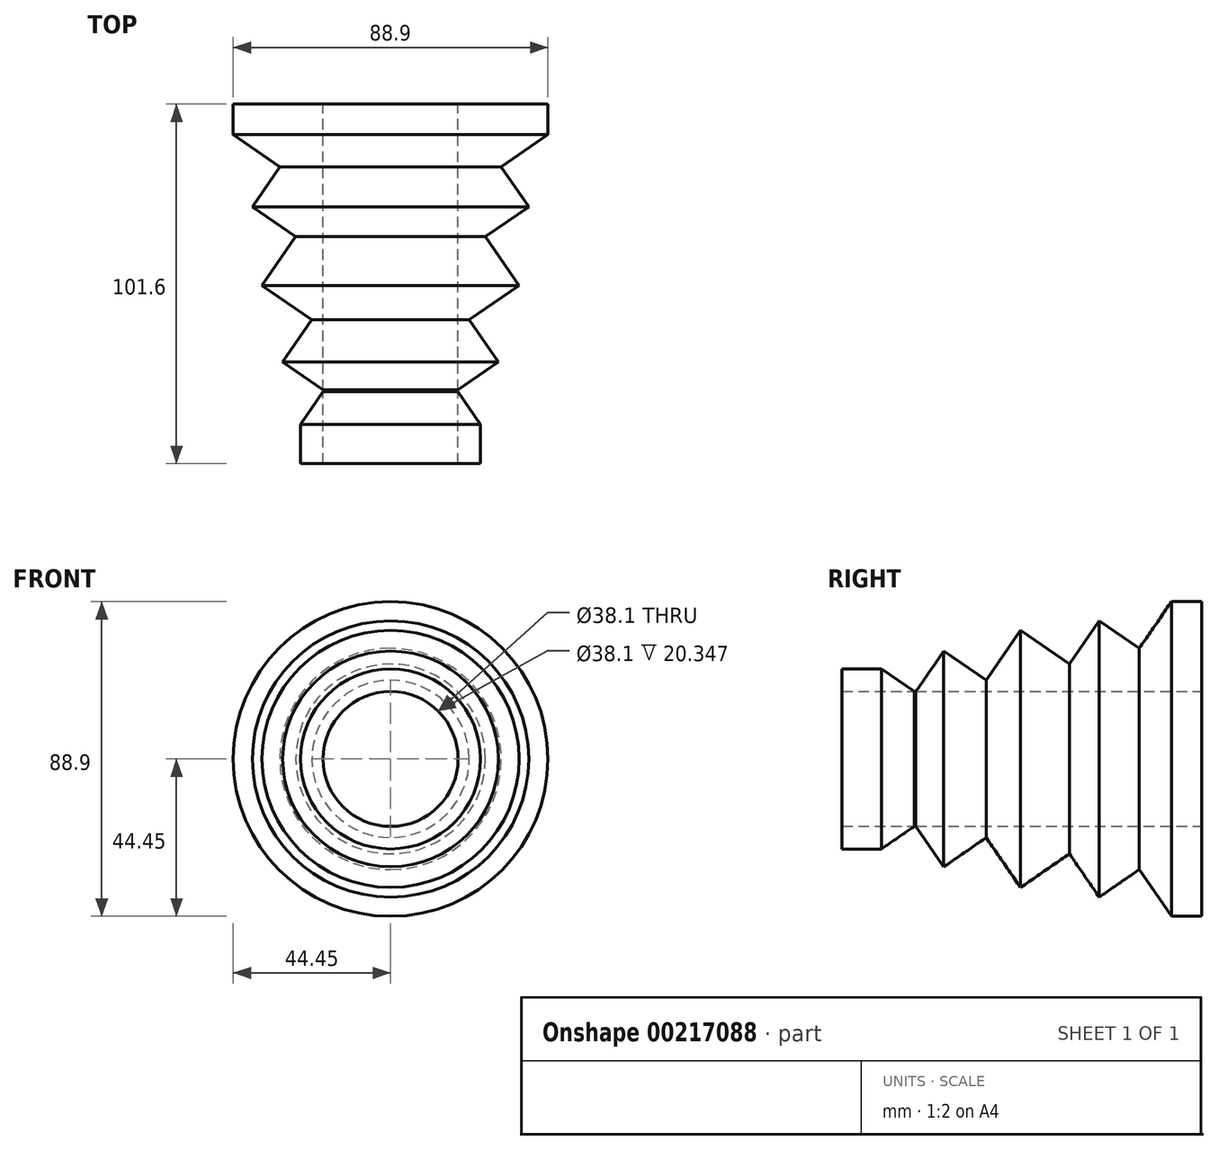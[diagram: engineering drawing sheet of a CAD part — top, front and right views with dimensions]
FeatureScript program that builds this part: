
annotation { "Feature Type Name" : "Feature", "Feature Type Description" : "" }
export const myFeature = defineFeature(function(context is Context, id is Id, definition is map)
    precondition{}
    {
        {
            var Q0;
            Q0=qCreatedBy(makeId("Front.planeOp"),FACE);
            var sketch = newSketch(context, id + "F0", { "sketchPlane" : qUnion([Q0])});
            skCircle(sketch, "E0", {"center": v(0, 0) * mm, "radius": 44.45 * mm});
            skCircle(sketch, "E1", {"center": v(0, 0) * mm, "radius": 19.05 * mm});
            skSolve(sketch);
        }
        {
            var Q0;
            Q0=makeQuery(id+"F0.imprint","IMPRINT",FACE,{"disambiguationData":[TD([[makeQuery(id+"F0.imprint","IMPRINT",EDGE,{"derivedFrom":sQuery(id+"F0.wireOp",EDGE,"E0")}),1.0]])]});
            extrude(context, id + "F1", {"entities" : qUnion([Q0]), "depth" : 101.6 * mm});
        }
        {
            var Q0;
            Q0=qCreatedBy(makeId("Top.planeOp"),FACE);
            var sketch = newSketch(context, id + "F2", { "sketchPlane" : qUnion([Q0])});
            skLineSegment(sketch, "E2", {"start": v(-45, 0) * mm, "end": v(-45, -8.22) * mm});
            skLineSegment(sketch, "E3", {"start": v(-45, -8.22) * mm, "end": v(-31.25, -17.7) * mm});
            skLineSegment(sketch, "E4", {"start": v(-31.25, -17.7) * mm, "end": v(-39.03, -28.99) * mm});
            skLineSegment(sketch, "E5", {"start": v(-39.03, -28.99) * mm, "end": v(-26.8, -37.42) * mm});
            skLineSegment(sketch, "E6", {"start": v(-26.8, -37.42) * mm, "end": v(-36.31, -51.22) * mm});
            skLineSegment(sketch, "E7", {"start": v(-36.31, -51.22) * mm, "end": v(-22.22, -60.93) * mm});
            skLineSegment(sketch, "E8", {"start": v(-22.22, -60.93) * mm, "end": v(-30.47, -72.9) * mm});
            skLineSegment(sketch, "E9", {"start": v(-30.47, -72.9) * mm, "end": v(-18.83, -80.93) * mm});
            skLineSegment(sketch, "E10", {"start": v(-18.83, -80.93) * mm, "end": v(-25.42, -90.49) * mm});
            skLineSegment(sketch, "E11", {"start": v(-25.42, -90.49) * mm, "end": v(-18.83, -102.04) * mm});
            skLineSegment(sketch, "E12", {"start": v(-25.42, -90.49) * mm, "end": v(-25.42, -107.53) * mm});
            skLineSegment(sketch, "E13", {"start": v(-25.42, -107.53) * mm, "end": v(-61.66, -107.53) * mm});
            skLineSegment(sketch, "E14", {"start": v(-61.66, -107.53) * mm, "end": v(-45, -8.22) * mm});
            skSolve(sketch);
        }
        {
            var Q0;
            Q0=makeQuery(id+"F2.imprint","IMPRINT",FACE,{"disambiguationData":[TD([[makeQuery(id+"F2.imprint","IMPRINT",EDGE,{"derivedFrom":sQuery(id+"F2.wireOp",EDGE,"E3")}),-1.0]])]});
            var Q1;
            Q1=makeQuery(id+"F1.opExtrude","CAP_EDGE",EDGE,{"disambiguationData":[OSD([sQuery(id+"F0.wireOp",EDGE,"E0")])],"isStart":true});
            revolve(context, id + "F3", {"operationType" : NewBodyOperationType.REMOVE, "entities" : qUnion([Q0]), "axis" : qUnion([Q1]), "revolveType" : RevolveType.FULL, "oppositeDirection" : true});
        }
    });
